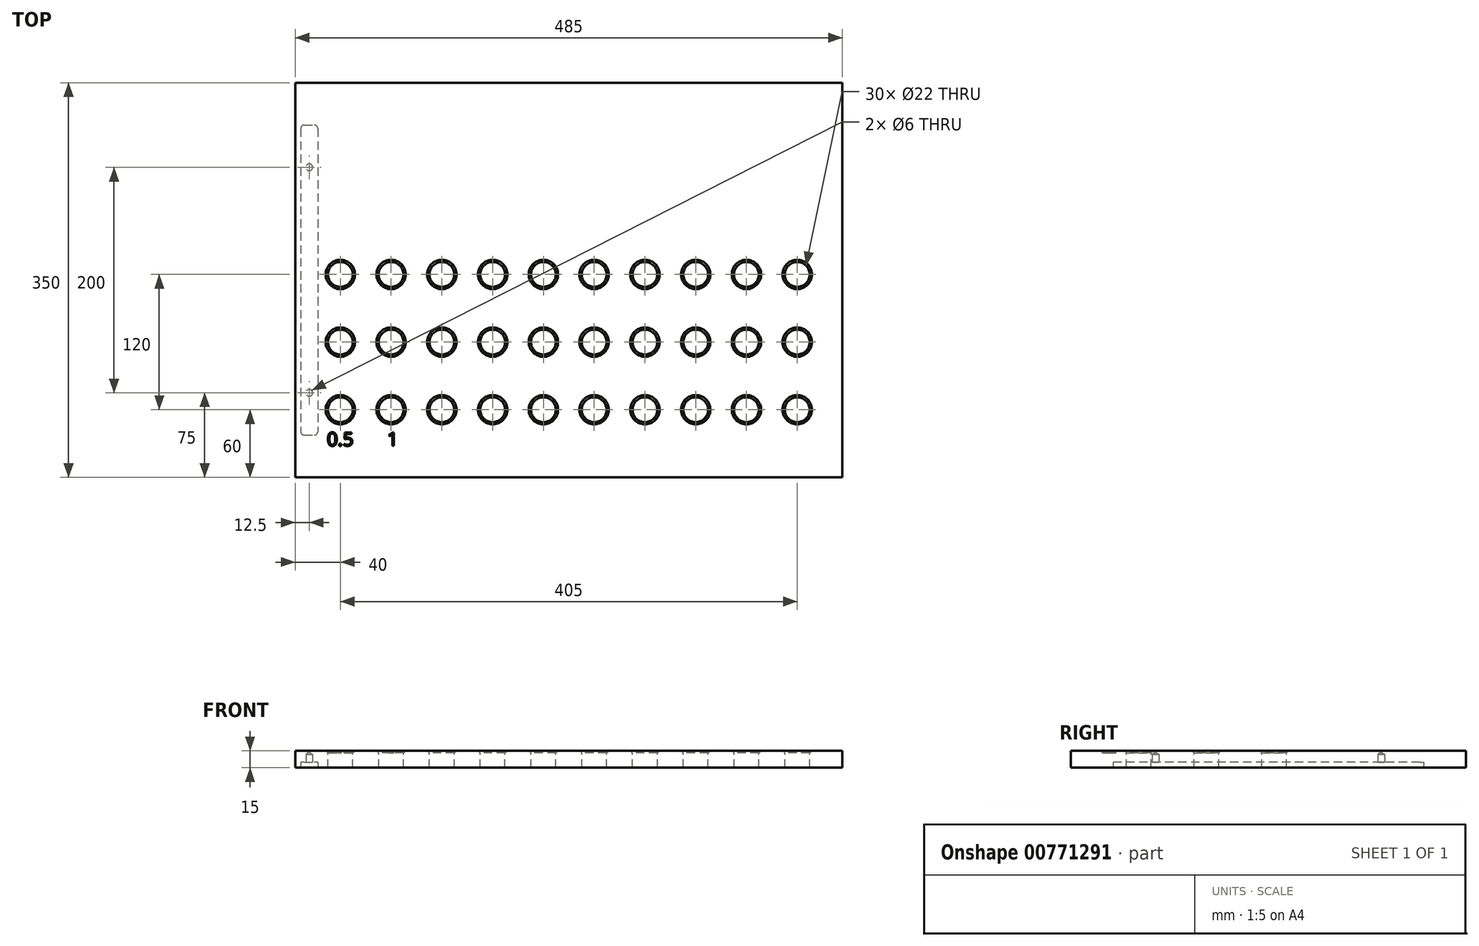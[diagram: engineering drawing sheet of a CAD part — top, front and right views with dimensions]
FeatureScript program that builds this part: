
annotation { "Feature Type Name" : "Feature", "Feature Type Description" : "" }
export const myFeature = defineFeature(function(context is Context, id is Id, definition is map)
    precondition{}
    {
        {
            var Q0;
            Q0=qCreatedBy(makeId("Top.planeOp"),FACE);
            var sketch = newSketch(context, id + "F0", { "sketchPlane" : qUnion([Q0])});
            skLineSegment(sketch, "E0.bottom", {"start": v(242.5, -175) * mm, "end": v(-242.5, -175) * mm});
            skLineSegment(sketch, "E0.top", {"start": v(242.5, 175) * mm, "end": v(-242.5, 175) * mm});
            skLineSegment(sketch, "E0.left", {"start": v(242.5, -175) * mm, "end": v(242.5, 175) * mm});
            skLineSegment(sketch, "E0.right", {"start": v(-242.5, -175) * mm, "end": v(-242.5, 175) * mm});
            skPoint(sketch, "E0.middle", {"position": v(0, 0) * mm});
            skPoint(sketch, "E1", {"position": v(-202.5, -115) * mm});
            skPoint(sketch, "E2.0.1.0", {"position": v(-202.5, -55) * mm});
            skPoint(sketch, "E2.0.2.0", {"position": v(-202.5, 5) * mm});
            skPoint(sketch, "E2.1.0.0", {"position": v(-157.5, -115) * mm});
            skPoint(sketch, "E2.1.1.0", {"position": v(-157.5, -55) * mm});
            skPoint(sketch, "E2.1.2.0", {"position": v(-157.5, 5) * mm});
            skPoint(sketch, "E2.2.0.0", {"position": v(-112.5, -115) * mm});
            skPoint(sketch, "E2.2.1.0", {"position": v(-112.5, -55) * mm});
            skPoint(sketch, "E2.2.2.0", {"position": v(-112.5, 5) * mm});
            skPoint(sketch, "E2.3.0.0", {"position": v(-67.5, -115) * mm});
            skPoint(sketch, "E2.3.1.0", {"position": v(-67.5, -55) * mm});
            skPoint(sketch, "E2.3.2.0", {"position": v(-67.5, 5) * mm});
            skPoint(sketch, "E2.4.0.0", {"position": v(-22.5, -115) * mm});
            skPoint(sketch, "E2.4.1.0", {"position": v(-22.5, -55) * mm});
            skPoint(sketch, "E2.4.2.0", {"position": v(-22.5, 5) * mm});
            skPoint(sketch, "E2.5.0.0", {"position": v(22.5, -115) * mm});
            skPoint(sketch, "E2.5.1.0", {"position": v(22.5, -55) * mm});
            skPoint(sketch, "E2.5.2.0", {"position": v(22.5, 5) * mm});
            skPoint(sketch, "E2.6.0.0", {"position": v(67.5, -115) * mm});
            skPoint(sketch, "E2.6.1.0", {"position": v(67.5, -55) * mm});
            skPoint(sketch, "E2.6.2.0", {"position": v(67.5, 5) * mm});
            skPoint(sketch, "E2.7.0.0", {"position": v(112.5, -115) * mm});
            skPoint(sketch, "E2.7.1.0", {"position": v(112.5, -55) * mm});
            skPoint(sketch, "E2.7.2.0", {"position": v(112.5, 5) * mm});
            skPoint(sketch, "E2.8.0.0", {"position": v(157.5, -115) * mm});
            skPoint(sketch, "E2.8.1.0", {"position": v(157.5, -55) * mm});
            skPoint(sketch, "E2.8.2.0", {"position": v(157.5, 5) * mm});
            skPoint(sketch, "E2.9.0.0", {"position": v(202.5, -115) * mm});
            skPoint(sketch, "E2.9.1.0", {"position": v(202.5, -55) * mm});
            skPoint(sketch, "E2.9.2.0", {"position": v(202.5, 5) * mm});
            skLineSegment(sketch, "E2.direction1", {"start": v(-202.5, -115) * mm, "end": v(-157.5, -115) * mm, "construction": true});
            skLineSegment(sketch, "E2.direction2", {"start": v(-202.5, -115) * mm, "end": v(-202.5, -55) * mm, "construction": true});
            skText(sketch, "E3", { "text": "0.5", "fontName": "OpenSans-Regular.ttf"});
            skText(sketch, "E4", { "text": "1", "fontName": "OpenSans-Regular.ttf"});
            const initialGuessF0  = {"E3": [-0.2143, -0.147, 1, 0, 0.012], "E4": [-0.16095, -0.147, 1, 0, 0.012]};
            skSetInitialGuess(sketch, initialGuessF0);
            skSolve(sketch);
        }
        {
            var Q0;
            Q0=makeQuery(id+"F0.imprint","IMPRINT",FACE,{"disambiguationData":[TD([[makeQuery(id+"F0.imprint","IMPRINT",EDGE,{"derivedFrom":sQuery(id+"F0.wireOp",EDGE,"E0.bottom")}),-1.0]])]});
            var Q1;
            Q1=makeQuery(id+"F0.imprint","IMPRINT",FACE,{"disambiguationData":[TD([[makeQuery(id+"F0.imprint","IMPRINT",EDGE,{"derivedFrom":sQuery(id+"F0.wireOp",EDGE,"E3.sketch_text.stroke-8")}),1.0]])]});
            var Q2;
            Q2=makeQuery(id+"F0.imprint","IMPRINT",FACE,{"disambiguationData":[TD([[makeQuery(id+"F0.imprint","IMPRINT",EDGE,{"derivedFrom":sQuery(id+"F0.wireOp",EDGE,"E3.sketch_text.stroke-0")}),-1.0]])]});
            var Q3;
            Q3=makeQuery(id+"F0.imprint","IMPRINT",FACE,{"disambiguationData":[TD([[makeQuery(id+"F0.imprint","IMPRINT",EDGE,{"derivedFrom":sQuery(id+"F0.wireOp",EDGE,"E3.sketch_text.stroke-24")}),-1.0]])]});
            var Q4;
            Q4=makeQuery(id+"F0.imprint","IMPRINT",FACE,{"disambiguationData":[TD([[makeQuery(id+"F0.imprint","IMPRINT",EDGE,{"derivedFrom":sQuery(id+"F0.wireOp",EDGE,"E3.sketch_text.stroke-16")}),-1.0]])]});
            var Q5;
            Q5=makeQuery(id+"F0.imprint","IMPRINT",FACE,{"disambiguationData":[TD([[makeQuery(id+"F0.imprint","IMPRINT",EDGE,{"derivedFrom":sQuery(id+"F0.wireOp",EDGE,"E4.sketch_text.stroke-0")}),-1.0]])]});
            extrude(context, id + "F1", {"entities" : qUnion([Q0, Q1, Q2, Q3, Q4, Q5]), "oppositeDirection" : true, "depth" : 15 * mm, "offsetDistance" : 25 * mm});
        }
        {
            var Q0;
            Q0=sQuery(id+"F0.wireOp",VERTEX,"E1");
            var Q1;
            Q1=makeQuery(id+"F1.opExtrude","SWEPT_BODY",BODY,{"disambiguationData":[OSD([sQuery(id+"F0.wireOp",EDGE,"E0.bottom"),sQuery(id+"F0.wireOp",EDGE,"E0.top"),sQuery(id+"F0.wireOp",EDGE,"E0.left"),sQuery(id+"F0.wireOp",EDGE,"E0.right")])]});
            hole(context, id + "F2", {"style" : HoleStyle.C_SINK, "endStyle" : HoleEndStyle.THROUGH, "holeDiameter" : 22 * mm, "cSinkDiameter" : 26 * mm, "cSinkAngle" : 90 * degree, "majorDiameter" : 5 * mm, "isTappedThrough" : true, "tappedDepth" : 12 * mm, "tapClearance" : 3, "locations" : qUnion([Q0]), "scope" : qUnion([Q1])});
        }
        {
            var Q0;
            Q0=sQuery(id+"F0.wireOp",VERTEX,"E2.1.0.0");
            var Q1;
            Q1=makeQuery(id+"F1.opExtrude","SWEPT_BODY",BODY,{"disambiguationData":[OSD([sQuery(id+"F0.wireOp",EDGE,"E0.bottom"),sQuery(id+"F0.wireOp",EDGE,"E0.top"),sQuery(id+"F0.wireOp",EDGE,"E0.left"),sQuery(id+"F0.wireOp",EDGE,"E0.right")])]});
            hole(context, id + "F3", {"style" : HoleStyle.C_SINK, "endStyle" : HoleEndStyle.THROUGH, "holeDiameter" : 22 * mm, "cSinkDiameter" : 26 * mm, "cSinkAngle" : 90 * degree, "majorDiameter" : 5 * mm, "isTappedThrough" : true, "tappedDepth" : 12 * mm, "tapClearance" : 3, "locations" : qUnion([Q0]), "scope" : qUnion([Q1])});
        }
        {
            var Q0;
            Q0=sQuery(id+"F0.wireOp",VERTEX,"E2.2.0.0");
            var Q1;
            Q1=makeQuery(id+"F1.opExtrude","SWEPT_BODY",BODY,{"disambiguationData":[OSD([sQuery(id+"F0.wireOp",EDGE,"E0.bottom"),sQuery(id+"F0.wireOp",EDGE,"E0.top"),sQuery(id+"F0.wireOp",EDGE,"E0.left"),sQuery(id+"F0.wireOp",EDGE,"E0.right")])]});
            hole(context, id + "F4", {"style" : HoleStyle.C_SINK, "endStyle" : HoleEndStyle.THROUGH, "holeDiameter" : 22 * mm, "cSinkDiameter" : 26 * mm, "cSinkAngle" : 90 * degree, "majorDiameter" : 5 * mm, "isTappedThrough" : true, "tappedDepth" : 12 * mm, "tapClearance" : 3, "locations" : qUnion([Q0]), "scope" : qUnion([Q1])});
        }
        {
            var Q0;
            Q0=sQuery(id+"F0.wireOp",VERTEX,"E2.3.0.0");
            var Q1;
            Q1=makeQuery(id+"F1.opExtrude","SWEPT_BODY",BODY,{"disambiguationData":[OSD([sQuery(id+"F0.wireOp",EDGE,"E0.bottom"),sQuery(id+"F0.wireOp",EDGE,"E0.top"),sQuery(id+"F0.wireOp",EDGE,"E0.left"),sQuery(id+"F0.wireOp",EDGE,"E0.right")])]});
            hole(context, id + "F5", {"style" : HoleStyle.C_SINK, "endStyle" : HoleEndStyle.THROUGH, "holeDiameter" : 22 * mm, "cSinkDiameter" : 26 * mm, "cSinkAngle" : 90 * degree, "majorDiameter" : 5 * mm, "isTappedThrough" : true, "tappedDepth" : 12 * mm, "tapClearance" : 3, "locations" : qUnion([Q0]), "scope" : qUnion([Q1])});
        }
        {
            var Q0;
            Q0=sQuery(id+"F0.wireOp",VERTEX,"E2.4.0.0");
            var Q1;
            Q1=makeQuery(id+"F1.opExtrude","SWEPT_BODY",BODY,{"disambiguationData":[OSD([sQuery(id+"F0.wireOp",EDGE,"E0.bottom"),sQuery(id+"F0.wireOp",EDGE,"E0.top"),sQuery(id+"F0.wireOp",EDGE,"E0.left"),sQuery(id+"F0.wireOp",EDGE,"E0.right")])]});
            hole(context, id + "F6", {"style" : HoleStyle.C_SINK, "endStyle" : HoleEndStyle.THROUGH, "holeDiameter" : 22 * mm, "cSinkDiameter" : 26 * mm, "cSinkAngle" : 90 * degree, "majorDiameter" : 5 * mm, "isTappedThrough" : true, "tappedDepth" : 12 * mm, "tapClearance" : 3, "locations" : qUnion([Q0]), "scope" : qUnion([Q1])});
        }
        {
            var Q0;
            Q0=sQuery(id+"F0.wireOp",VERTEX,"E2.5.0.0");
            var Q1;
            Q1=makeQuery(id+"F1.opExtrude","SWEPT_BODY",BODY,{"disambiguationData":[OSD([sQuery(id+"F0.wireOp",EDGE,"E0.bottom"),sQuery(id+"F0.wireOp",EDGE,"E0.top"),sQuery(id+"F0.wireOp",EDGE,"E0.left"),sQuery(id+"F0.wireOp",EDGE,"E0.right")])]});
            hole(context, id + "F7", {"style" : HoleStyle.C_SINK, "endStyle" : HoleEndStyle.THROUGH, "holeDiameter" : 22 * mm, "cSinkDiameter" : 26 * mm, "cSinkAngle" : 90 * degree, "majorDiameter" : 5 * mm, "isTappedThrough" : true, "tappedDepth" : 12 * mm, "tapClearance" : 3, "locations" : qUnion([Q0]), "scope" : qUnion([Q1])});
        }
        {
            var Q0;
            Q0=sQuery(id+"F0.wireOp",VERTEX,"E2.6.0.0");
            var Q1;
            Q1=sQuery(id+"F0.wireOp",VERTEX,"E2.7.0.0");
            var Q2;
            Q2=sQuery(id+"F0.wireOp",VERTEX,"E2.8.0.0");
            var Q3;
            Q3=sQuery(id+"F0.wireOp",VERTEX,"E2.8.1.0");
            var Q4;
            Q4=sQuery(id+"F0.wireOp",VERTEX,"E2.7.1.0");
            var Q5;
            Q5=sQuery(id+"F0.wireOp",VERTEX,"E2.6.1.0");
            var Q6;
            Q6=sQuery(id+"F0.wireOp",VERTEX,"E2.5.1.0");
            var Q7;
            Q7=sQuery(id+"F0.wireOp",VERTEX,"E2.4.1.0");
            var Q8;
            Q8=sQuery(id+"F0.wireOp",VERTEX,"E2.3.1.0");
            var Q9;
            Q9=sQuery(id+"F0.wireOp",VERTEX,"E2.2.1.0");
            var Q10;
            Q10=sQuery(id+"F0.wireOp",VERTEX,"E2.1.1.0");
            var Q11;
            Q11=sQuery(id+"F0.wireOp",VERTEX,"E2.0.1.0");
            var Q12;
            Q12=sQuery(id+"F0.wireOp",VERTEX,"E2.0.2.0");
            var Q13;
            Q13=sQuery(id+"F0.wireOp",VERTEX,"E2.1.2.0");
            var Q14;
            Q14=sQuery(id+"F0.wireOp",VERTEX,"E2.2.2.0");
            var Q15;
            Q15=sQuery(id+"F0.wireOp",VERTEX,"E2.3.2.0");
            var Q16;
            Q16=sQuery(id+"F0.wireOp",VERTEX,"E2.4.2.0");
            var Q17;
            Q17=sQuery(id+"F0.wireOp",VERTEX,"E2.5.2.0");
            var Q18;
            Q18=sQuery(id+"F0.wireOp",VERTEX,"E2.6.2.0");
            var Q19;
            Q19=sQuery(id+"F0.wireOp",VERTEX,"E2.7.2.0");
            var Q20;
            Q20=sQuery(id+"F0.wireOp",VERTEX,"E2.8.2.0");
            var Q21;
            Q21=sQuery(id+"F0.wireOp",VERTEX,"E2.9.2.0");
            var Q22;
            Q22=sQuery(id+"F0.wireOp",VERTEX,"E2.9.1.0");
            var Q23;
            Q23=sQuery(id+"F0.wireOp",VERTEX,"E2.9.0.0");
            var Q24;
            Q24=makeQuery(id+"F1.opExtrude","SWEPT_BODY",BODY,{"disambiguationData":[OSD([sQuery(id+"F0.wireOp",EDGE,"E0.bottom"),sQuery(id+"F0.wireOp",EDGE,"E0.top"),sQuery(id+"F0.wireOp",EDGE,"E0.left"),sQuery(id+"F0.wireOp",EDGE,"E0.right")])]});
            hole(context, id + "F8", {"style" : HoleStyle.C_SINK, "endStyle" : HoleEndStyle.THROUGH, "holeDiameter" : 22 * mm, "cSinkDiameter" : 26 * mm, "cSinkAngle" : 90 * degree, "majorDiameter" : 5 * mm, "isTappedThrough" : true, "tappedDepth" : 12 * mm, "tapClearance" : 3, "locations" : qUnion([Q0, Q1, Q2, Q3, Q4, Q5, Q6, Q7, Q8, Q9, Q10, Q11, Q12, Q13, Q14, Q15, Q16, Q17, Q18, Q19, Q20, Q21, Q22, Q23]), "scope" : qUnion([Q24])});
        }
        {
            var Q0;
            Q0=makeQuery(id+"F0.imprint","IMPRINT",FACE,{"disambiguationData":[TD([[makeQuery(id+"F0.imprint","IMPRINT",EDGE,{"derivedFrom":sQuery(id+"F0.wireOp",EDGE,"E3.sketch_text.stroke-0")}),-1.0]])]});
            var Q1;
            Q1=makeQuery(id+"F0.imprint","IMPRINT",FACE,{"disambiguationData":[TD([[makeQuery(id+"F0.imprint","IMPRINT",EDGE,{"derivedFrom":sQuery(id+"F0.wireOp",EDGE,"E3.sketch_text.stroke-16")}),-1.0]])]});
            var Q2;
            Q2=makeQuery(id+"F0.imprint","IMPRINT",FACE,{"disambiguationData":[TD([[makeQuery(id+"F0.imprint","IMPRINT",EDGE,{"derivedFrom":sQuery(id+"F0.wireOp",EDGE,"E3.sketch_text.stroke-24")}),-1.0]])]});
            var Q3;
            Q3=makeQuery(id+"F0.imprint","IMPRINT",FACE,{"disambiguationData":[TD([[makeQuery(id+"F0.imprint","IMPRINT",EDGE,{"derivedFrom":sQuery(id+"F0.wireOp",EDGE,"E4.sketch_text.stroke-0")}),-1.0]])]});
            extrude(context, id + "F9", {"entities" : qUnion([Q0, Q1, Q2, Q3]), "operationType" : NewBodyOperationType.REMOVE, "oppositeDirection" : true, "depth" : 2 * mm, "offsetDistance" : 25 * mm});
        }
        {
            var Q0;
            Q0=makeQuery(id+"F1.opExtrude","CAP_FACE",FACE,{"disambiguationData":[OSD([sQuery(id+"F0.wireOp",EDGE,"E0.bottom"),sQuery(id+"F0.wireOp",EDGE,"E0.top"),sQuery(id+"F0.wireOp",EDGE,"E0.left"),sQuery(id+"F0.wireOp",EDGE,"E0.right")])],"isStart":false});
            cPlane(context, id + "F10", {"entities" : qUnion([Q0]), "cplaneType" : CPlaneType.OFFSET, "offset" : 0 * mm, "width" : 150 * mm, "height" : 150 * mm});
        }
        {
            var Q0;
            Q0=qCreatedBy(id+"F10.planeOp",FACE);
            var sketch = newSketch(context, id + "F11", { "sketchPlane" : qUnion([Q0])});
            skPoint(sketch, "E5", {"position": v(-230, 100) * mm});
            skPoint(sketch, "E6", {"position": v(-230, -100) * mm});
            skLineSegment(sketch, "E7.bottom", {"start": v(-234.5, -137.5) * mm, "end": v(-225.5, -137.5) * mm});
            skLineSegment(sketch, "E7.top", {"start": v(-234.5, 137.5) * mm, "end": v(-225.5, 137.5) * mm});
            skLineSegment(sketch, "E7.left", {"start": v(-237.5, -134.5) * mm, "end": v(-237.5, 134.5) * mm});
            skLineSegment(sketch, "E7.right", {"start": v(-222.5, -134.5) * mm, "end": v(-222.5, 134.5) * mm});
            skPoint(sketch, "E8.visualSharp", {"position": v(-222.5, 137.5) * mm});
            skArc(sketch, "E8.filletArc", {"start": v(-222.5, 134.5) * mm, "mid": v(-223.38, 136.62) * mm, "end": v(-225.5, 137.5) * mm});
            skPoint(sketch, "E9.visualSharp", {"position": v(-237.5, 137.5) * mm});
            skArc(sketch, "E9.filletArc", {"start": v(-234.5, 137.5) * mm, "mid": v(-236.62, 136.62) * mm, "end": v(-237.5, 134.5) * mm});
            skPoint(sketch, "E10.visualSharp", {"position": v(-222.5, -137.5) * mm});
            skArc(sketch, "E10.filletArc", {"start": v(-225.5, -137.5) * mm, "mid": v(-223.38, -136.62) * mm, "end": v(-222.5, -134.5) * mm});
            skPoint(sketch, "E11.visualSharp", {"position": v(-237.5, -137.5) * mm});
            skArc(sketch, "E11.filletArc", {"start": v(-237.5, -134.5) * mm, "mid": v(-236.62, -136.62) * mm, "end": v(-234.5, -137.5) * mm});
            skSolve(sketch);
        }
        {
            var Q0;
            Q0=makeQuery(id+"F11.imprint","IMPRINT",FACE,{"disambiguationData":[TD([[makeQuery(id+"F11.imprint","IMPRINT",EDGE,{"derivedFrom":sQuery(id+"F11.wireOp",EDGE,"E7.bottom")}),1.0]])]});
            extrude(context, id + "F12", {"entities" : qUnion([Q0]), "operationType" : NewBodyOperationType.REMOVE, "oppositeDirection" : true, "depth" : 5 * mm, "offsetDistance" : 25 * mm});
        }
        {
            var Q0;
            Q0=sQuery(id+"F11.wireOp",VERTEX,"E5");
            var Q1;
            Q1=sQuery(id+"F11.wireOp",VERTEX,"E6");
            var Q2;
            Q2=makeQuery(id+"F1.opExtrude","SWEPT_BODY",BODY,{"disambiguationData":[OSD([sQuery(id+"F0.wireOp",EDGE,"E0.bottom"),sQuery(id+"F0.wireOp",EDGE,"E0.top"),sQuery(id+"F0.wireOp",EDGE,"E0.left"),sQuery(id+"F0.wireOp",EDGE,"E0.right")])]});
            hole(context, id + "F13", {"style" : HoleStyle.SIMPLE, "endStyle" : HoleEndStyle.BLIND, "holeDiameter" : 6 * mm, "majorDiameter" : 5 * mm, "holeDepth" : 7 * mm, "isTappedThrough" : true, "tappedDepth" : 12 * mm, "tapClearance" : 3, "locations" : qUnion([Q0, Q1]), "scope" : qUnion([Q2])});
        }
    });
